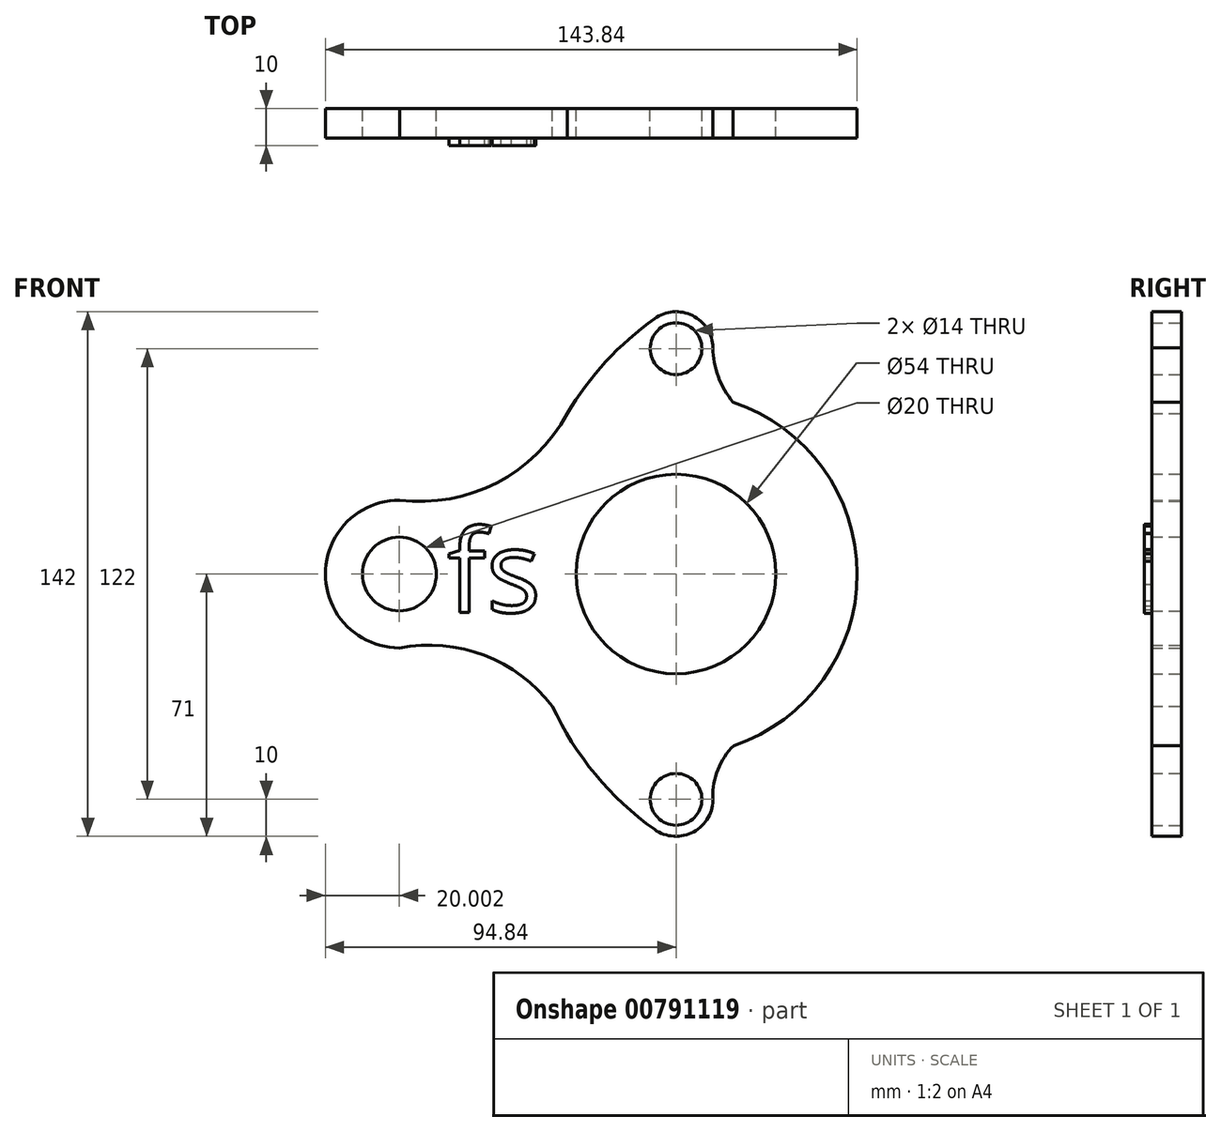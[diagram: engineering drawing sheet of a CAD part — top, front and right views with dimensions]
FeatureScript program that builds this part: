
annotation { "Feature Type Name" : "Feature", "Feature Type Description" : "" }
export const myFeature = defineFeature(function(context is Context, id is Id, definition is map)
    precondition{}
    {
        {
            var Q0;
            Q0=qCreatedBy(makeId("Front.planeOp"),FACE);
            var sketch = newSketch(context, id + "F0", { "sketchPlane" : qUnion([Q0])});
            skCircle(sketch, "E0", {"center": v(0, 0) * mm, "radius": 27 * mm});
            skArc(sketch, "E1", {"start": v(-38.6, -30.18) * mm, "mid": v(-36.14, -33.09) * mm, "end": v(-33.46, -35.8) * mm});
            skLineSegment(sketch, "E2", {"start": v(0, 0) * mm, "end": v(0, -57.36) * mm});
            skLineSegment(sketch, "E3", {"start": v(0, 0) * mm, "end": v(0, 61) * mm});
            skLineSegment(sketch, "E4", {"start": v(0, 0) * mm, "end": v(0, -61) * mm});
            skCircle(sketch, "E5", {"center": v(0, 61) * mm, "radius": 7 * mm});
            skCircle(sketch, "E6", {"center": v(0, -61) * mm, "radius": 7 * mm});
            skCircle(sketch, "E7", {"center": v(0, 61) * mm, "radius": 10 * mm});
            skCircle(sketch, "E8", {"center": v(0, -61) * mm, "radius": 10 * mm});
            skLineSegment(sketch, "E9", {"start": v(0, 0) * mm, "end": v(-83.67, -7.45) * mm});
            skArc(sketch, "E10", {"start": v(-5.82, 69.13) * mm, "mid": v(-21.8, 54.26) * mm, "end": v(-33.46, 35.8) * mm});
            skArc(sketch, "E11", {"start": v(-71.44, 19.7) * mm, "mid": v(-94.82, -0.89) * mm, "end": v(-69.7, -19.33) * mm});
            skCircle(sketch, "E12", {"center": v(-74.84, 0) * mm, "radius": 10 * mm});
            skArc(sketch, "E13", {"start": v(-74.8, 20) * mm, "mid": v(-48.5, 24.7) * mm, "end": v(-29.44, 43.42) * mm});
            skArc(sketch, "E14", {"start": v(-33.46, -35.8) * mm, "mid": v(-51.9, -22) * mm, "end": v(-74.85, -20) * mm});
            skArc(sketch, "E15", {"start": v(15.63, -46.44) * mm, "mid": v(11.3, -52.9) * mm, "end": v(10, -60.57) * mm});
            skArc(sketch, "E16", {"start": v(10, 61.27) * mm, "mid": v(11.42, 53.4) * mm, "end": v(15.46, 46.5) * mm});
            skArc(sketch, "E17.trimOffspring", {"start": v(-33.46, -35.8) * mm, "mid": v(-21.8, -54.26) * mm, "end": v(-5.82, -69.13) * mm});
            skArc(sketch, "E18.trimOffspring", {"start": v(15.63, -46.44) * mm, "mid": v(49, 0.09) * mm, "end": v(15.46, 46.5) * mm});
            skSolve(sketch);
        }
        {
            var Q0;
            {var subQ13=sQuery(id+"F0.wireOp",EDGE,"E17.trimOffspring");Q0=makeQuery(id+"F0.imprint","IMPRINT",FACE,{"disambiguationData":[TD([[makeQuery(id+"F0.imprint","IMPRINT",EDGE,{"derivedFrom":subQ13}),1.0]])]});}
            var Q1;
            {var subQ12=sQuery(id+"F0.wireOp",EDGE,"E15");Q1=makeQuery(id+"F0.imprint","IMPRINT",FACE,{"disambiguationData":[TD([[makeQuery(id+"F0.imprint","IMPRINT",EDGE,{"derivedFrom":subQ12}),-1.0]])]});}
            var Q2;
            Q2=makeQuery(id+"F0.imprint","IMPRINT",FACE,{"disambiguationData":[TD([[makeQuery(id+"F0.imprint","IMPRINT",EDGE,{"derivedFrom":sQuery(id+"F0.wireOp",EDGE,"E5")}),-1.0]])]});
            var Q3;
            Q3=makeQuery(id+"F0.imprint","IMPRINT",FACE,{"disambiguationData":[TD([[makeQuery(id+"F0.imprint","IMPRINT",EDGE,{"derivedFrom":sQuery(id+"F0.wireOp",EDGE,"E6")}),-1.0]])]});
            extrude(context, id + "F1", {"entities" : qUnion([Q0, Q1, Q2, Q3]), "depth" : 8 * mm, "offsetDistance" : 25 * mm});
        }
        {
            var Q0;
            Q0=makeQuery(id+"F1.opExtrude","CAP_FACE",FACE,{"disambiguationData":[OSD([sQuery(id+"F0.wireOp",EDGE,"E0"),sQuery(id+"F0.wireOp",EDGE,"E5"),sQuery(id+"F0.wireOp",EDGE,"E6"),sQuery(id+"F0.wireOp",EDGE,"E7"),sQuery(id+"F0.wireOp",EDGE,"E8"),sQuery(id+"F0.wireOp",EDGE,"E10"),sQuery(id+"F0.wireOp",EDGE,"E11"),sQuery(id+"F0.wireOp",EDGE,"E12"),sQuery(id+"F0.wireOp",EDGE,"E13"),sQuery(id+"F0.wireOp",EDGE,"E14"),sQuery(id+"F0.wireOp",EDGE,"E15"),sQuery(id+"F0.wireOp",EDGE,"E16"),sQuery(id+"F0.wireOp",EDGE,"E17.trimOffspring"),sQuery(id+"F0.wireOp",EDGE,"E18.trimOffspring")])],"isStart":false});
            var sketch = newSketch(context, id + "F2", { "sketchPlane" : qUnion([Q0])});
            skText(sketch, "E19", { "text": "fs", "fontName": "OpenSans-Regular.ttf"});
            const initialGuessF2  = {"E19": [-0.0619, -0.01034, 1, 0, 0.02238]};
            skSetInitialGuess(sketch, initialGuessF2);
            skSolve(sketch);
        }
        {
            var Q0;
            Q0 = qSketchRegion(id + "F2", true);
            extrude(context, id + "F3", {"entities" : qUnion([Q0]), "operationType" : NewBodyOperationType.ADD, "depth" : 2 * mm, "offsetDistance" : 25 * mm});
        }
    });
